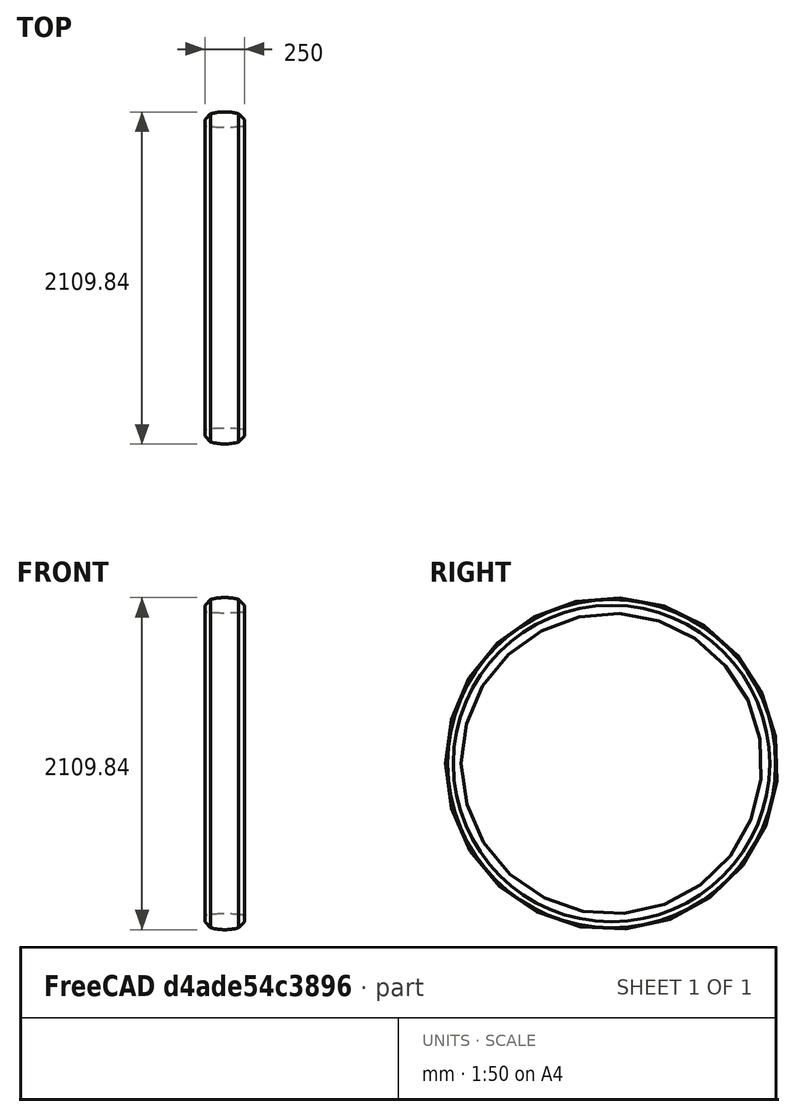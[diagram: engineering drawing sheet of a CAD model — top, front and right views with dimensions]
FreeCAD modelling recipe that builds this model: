
FCSTD DOCUMENT
Label: PR_006
objects: Sketcher::SketchObject×1, PartDesign::Revolution×1
note: 3 computed .brp shape members not serialized (recipe doc carries the construction recipe); baked Part::Feature solids carry a one-line shape summary decoded from their .brp

FEATURE [Sketcher::SketchObject] Sketch
  sketch-geometry (10):
    g0: LineSegment [constr] StartX=-66.7293 StartY=-954.92 StartZ=0 EndX=292.304 EndY=-954.92 EndZ=0
    g1: LineSegment StartX=250 StartY=-976.549 StartZ=0 EndX=250 EndY=-1004.92 EndZ=0
    g2: LineSegment StartX=0 StartY=-976.549 StartZ=0 EndX=0 EndY=-1004.92 EndZ=0
    g3: LineSegment [constr] StartX=-37.7609 StartY=-1054.92 StartZ=0 EndX=266.72 EndY=-1054.92 EndZ=0
    g4: LineSegment StartX=0 StartY=-1004.92 StartZ=0 EndX=36.2899 EndY=-1042.5 EndZ=0
    g5: LineSegment StartX=250 StartY=-1004.92 StartZ=0 EndX=213.71 EndY=-1042.5 EndZ=0
    g6: ArcOfCircle CenterX=15 CenterY=-976.549 CenterZ=0 NormalX=0 NormalY=0 NormalZ=1 Radius=15 StartAngle=1.69117 EndAngle=3.14159
    g7: ArcOfCircle CenterX=235 CenterY=-976.549 CenterZ=0 NormalX=0 NormalY=0 NormalZ=1 Radius=15 StartAngle=0 EndAngle=1.45042
    g8: ArcOfCircle CenterX=125 CenterY=-1885.92 CenterZ=0 NormalX=0 NormalY=0 NormalZ=1 Radius=931 StartAngle=1.45042 EndAngle=1.69117
    g9: ArcOfCircle CenterX=125 CenterY=-731.92 CenterZ=0 NormalX=0 NormalY=0 NormalZ=1 Radius=323 StartAngle=4.43417 EndAngle=4.99061
  constraints (28):
    c: Horizontal(g0)
    c: DistanceY(g0) = -954.92
    c: Vertical(g1)
    c: Vertical(g2)
    c: Tangent(g2,g-2)
    c: DistanceX(g1,g2) = -250
    c: Horizontal(g3)
    c: DistanceY(g0,g3) = -100
    c: Coincident(g5,g1)
    c: Coincident(g2,g4)
    c: Radius(g6) = 15
    c: Radius(g7) = 15
    c: Tangent(g2,g6)
    c: Tangent(g7,g1)
    c: Radius(g8) = 931
    c: Tangent(g6,g8)
    c: Tangent(g7,g8)
    c: Tangent(g0,g8)
    c: DistanceX(g8) = 125
    c: Angle(g1,g5) = 2.37365
    c: Angle(g4,g2) = 2.37365
    c: Radius(g9) = 323
    c: DistanceX(g9) = 125
    c: Tangent(g9,g3)
    c: Coincident(g9,g5)
    c: Coincident(g4,g9)
    c: DistanceY(g2,g3) = -50
    c: DistanceY(g1,g3) = -50
FEATURE [PartDesign::Revolution] Revolution
  Angle = 360
  Axis = (1,0,0)
  Base = (0,0,0)
  ReferenceAxis = -> Sketch [H_Axis]
  Sketch = -> Sketch
